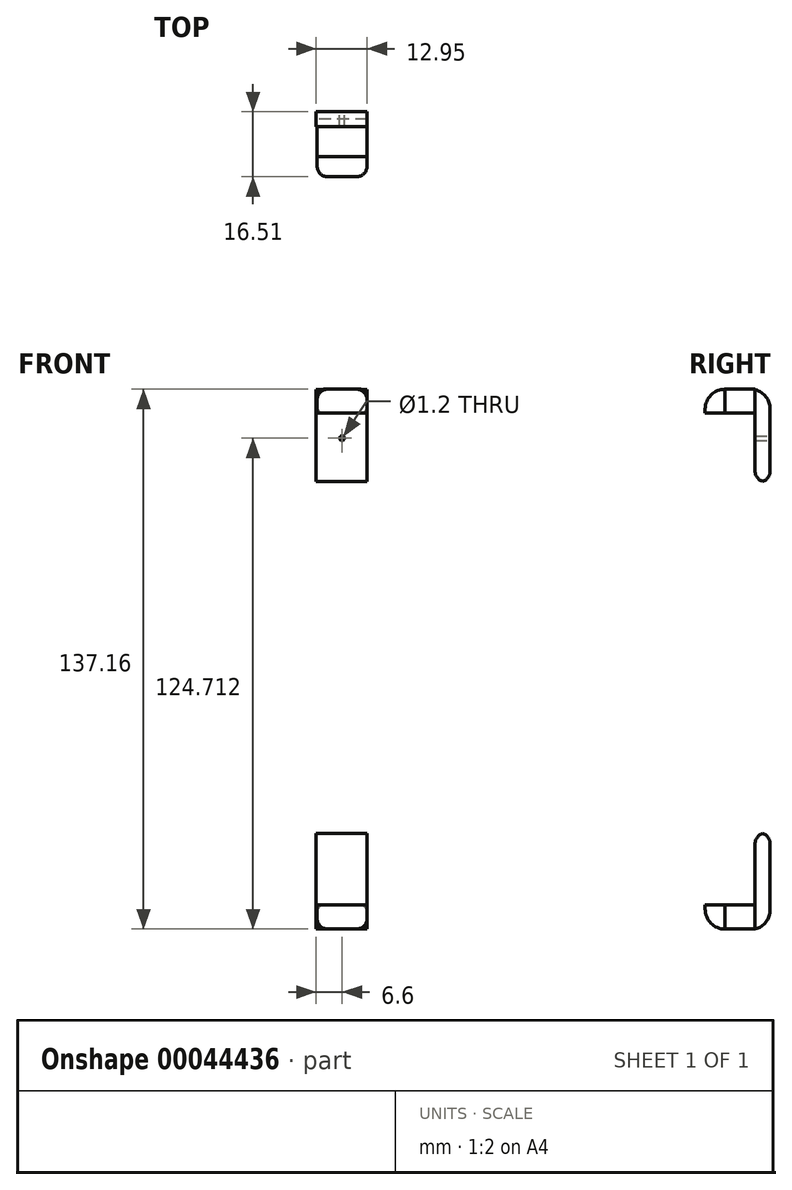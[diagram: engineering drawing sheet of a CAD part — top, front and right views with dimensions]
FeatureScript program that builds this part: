
annotation { "Feature Type Name" : "Feature", "Feature Type Description" : "" }
export const myFeature = defineFeature(function(context is Context, id is Id, definition is map)
    precondition{}
    {
        {
            var Q0;
            Q0=qCreatedBy(makeId("Front.planeOp"),FACE);
            var sketch = newSketch(context, id + "F0", { "sketchPlane" : qUnion([Q0])});
            skLineSegment(sketch, "E0.rect.bottom", {"start": v(-6.35, 68.58) * mm, "end": v(6.35, 68.58) * mm});
            skLineSegment(sketch, "E0.rect.top", {"start": v(-6.35, -68.58) * mm, "end": v(6.35, -68.58) * mm});
            skLineSegment(sketch, "E0.rect.left", {"start": v(-6.35, 68.58) * mm, "end": v(-6.35, -68.58) * mm});
            skLineSegment(sketch, "E0.rect.right", {"start": v(6.35, 68.58) * mm, "end": v(6.35, -68.58) * mm});
            skPoint(sketch, "E0.rect.middle", {"position": v(0, 0) * mm});
            skLineSegment(sketch, "E1.rect.bottom", {"start": v(0, 62.48) * mm, "end": v(0, 62.48) * mm});
            skLineSegment(sketch, "E1.rect.top", {"start": v(0, -62.48) * mm, "end": v(0, -62.48) * mm});
            skLineSegment(sketch, "E1.rect.left", {"start": v(0, 62.48) * mm, "end": v(0, -62.48) * mm});
            skLineSegment(sketch, "E1.rect.right", {"start": v(0, 62.48) * mm, "end": v(0, -62.48) * mm});
            skLineSegment(sketch, "E2", {"start": v(0, 62.48) * mm, "end": v(-6.35, 62.48) * mm});
            skLineSegment(sketch, "E3", {"start": v(-6.35, 62.48) * mm, "end": v(6.35, 62.48) * mm});
            skLineSegment(sketch, "E4", {"start": v(-6.35, -62.48) * mm, "end": v(6.35, -62.48) * mm});
            skSolve(sketch);
        }
        {
            var Q0;
            {var subQ4=sQuery(id+"F0.wireOp",EDGE,"E0.rect.top");Q0=makeQuery(id+"F0.imprint","IMPRINT",FACE,{"disambiguationData":[TD([[makeQuery(id+"F0.imprint","IMPRINT",EDGE,{"derivedFrom":subQ4}),1.0]])]});}
            var Q1;
            {var subQ4=sQuery(id+"F0.wireOp",EDGE,"E0.rect.bottom");Q1=makeQuery(id+"F0.imprint","IMPRINT",FACE,{"disambiguationData":[TD([[makeQuery(id+"F0.imprint","IMPRINT",EDGE,{"derivedFrom":subQ4}),-1.0]])]});}
            extrude(context, id + "F1", {"entities" : qUnion([Q0, Q1]), "oppositeDirection" : true, "depth" : 7.62 * mm});
        }
        {
            var Q0;
            {var subQ3=sQuery(id+"F0.wireOp",EDGE,"E1.rect.right");Q0=makeQuery(id+"F0.imprint","IMPRINT",FACE,{"disambiguationData":[TD([[makeQuery(id+"F0.imprint","IMPRINT",EDGE,{"derivedFrom":subQ3}),1.0]])]});}
            var Q1;
            {var subQ3=sQuery(id+"F0.wireOp",EDGE,"E1.rect.right");Q1=makeQuery(id+"F0.imprint","IMPRINT",FACE,{"disambiguationData":[TD([[makeQuery(id+"F0.imprint","IMPRINT",EDGE,{"derivedFrom":subQ3}),-1.0]])]});}
            var Q2;
            {var subQ4=sQuery(id+"F0.wireOp",EDGE,"E0.rect.top");Q2=makeQuery(id+"F0.imprint","IMPRINT",FACE,{"disambiguationData":[TD([[makeQuery(id+"F0.imprint","IMPRINT",EDGE,{"derivedFrom":subQ4}),1.0]])]});}
            var Q3;
            {var subQ4=sQuery(id+"F0.wireOp",EDGE,"E0.rect.bottom");Q3=makeQuery(id+"F0.imprint","IMPRINT",FACE,{"disambiguationData":[TD([[makeQuery(id+"F0.imprint","IMPRINT",EDGE,{"derivedFrom":subQ4}),-1.0]])]});}
            extrude(context, id + "F2", {"entities" : qUnion([Q0, Q1, Q2, Q3]), "depth" : 5.08 * mm});
        }
        {
            var Q0;
            Q0=makeQuery(id+"F1.opExtrude","CAP_FACE",FACE,{"disambiguationData":[OSD([sQuery(id+"F0.wireOp",EDGE,"E0.rect.top"),sQuery(id+"F0.wireOp",EDGE,"E0.rect.left"),sQuery(id+"F0.wireOp",EDGE,"E0.rect.right"),sQuery(id+"F0.wireOp",EDGE,"E4")])],"isStart":false});
            var sketch = newSketch(context, id + "F3", { "sketchPlane" : qUnion([Q0])});
            skLineSegment(sketch, "E5.bottom", {"start": v(-6.35, -68.58) * mm, "end": v(6.6, -68.58) * mm});
            skLineSegment(sketch, "E5.top", {"start": v(-6.35, 68.46) * mm, "end": v(6.6, 68.46) * mm});
            skLineSegment(sketch, "E5.left", {"start": v(-6.35, -68.58) * mm, "end": v(-6.35, 68.46) * mm});
            skLineSegment(sketch, "E5.right", {"start": v(6.6, -68.58) * mm, "end": v(6.6, 68.46) * mm});
            skLineSegment(sketch, "E6.bottom", {"start": v(-6.35, 45.07) * mm, "end": v(6.6, 45.07) * mm});
            skLineSegment(sketch, "E6.top", {"start": v(-6.35, -44.2) * mm, "end": v(6.6, -44.2) * mm});
            skLineSegment(sketch, "E6.left", {"start": v(-6.35, 45.07) * mm, "end": v(-6.35, -44.2) * mm});
            skLineSegment(sketch, "E6.right", {"start": v(6.6, 45.07) * mm, "end": v(6.6, -44.2) * mm});
            skSolve(sketch);
        }
        {
            var Q0;
            {var subQ7=sQuery(id+"F3.wireOp",EDGE,"E6.top");Q0=makeQuery(id+"F3.imprint","IMPRINT",FACE,{"disambiguationData":[TD([[makeQuery(id+"F3.imprint","IMPRINT",EDGE,{"derivedFrom":subQ7}),-1.0]])]});}
            var Q1;
            {var subQ0=sQuery(id+"F0.wireOp",EDGE,"E4");var subQ1=makeQuery(id+"F1.opExtrude","CAP_EDGE",EDGE,{"disambiguationData":[OSD([subQ0])],"isStart":false});Q1=makeQuery(id+"F3.imprint","IMPRINT",FACE,{"disambiguationData":[TD([[makeQuery(id+"F3.imprint","IMPRINT",EDGE,{"derivedFrom":subQ1}),1.0]])]});}
            var Q2;
            {var subQ2=sQuery(id+"F3.wireOp",EDGE,"E5.top");Q2=makeQuery(id+"F3.imprint","IMPRINT",FACE,{"disambiguationData":[TD([[makeQuery(id+"F3.imprint","IMPRINT",EDGE,{"derivedFrom":subQ2}),-1.0]])]});}
            extrude(context, id + "F4", {"entities" : qUnion([Q0, Q1, Q2]), "depth" : 3.8 * mm});
        }
        {
            var Q0;
            Q0=makeQuery(id+"F4.opExtrude","CAP_FACE",FACE,{"disambiguationData":[OSD([sQuery(id+"F3.wireOp",EDGE,"E5.top"),sQuery(id+"F3.wireOp",EDGE,"E5.left"),sQuery(id+"F3.wireOp",EDGE,"E5.right"),sQuery(id+"F3.wireOp",EDGE,"E6.bottom")])],"isStart":false});
            var sketch = newSketch(context, id + "F5", { "sketchPlane" : qUnion([Q0])});
            skLineSegment(sketch, "E7", {"start": v(0.1, 62.23) * mm, "end": v(0, 56.13) * mm});
            skCircle(sketch, "E8", {"center": v(0, 56.13) * mm, "radius": 0.6 * mm});
            skSolve(sketch);
        }
        {
            var Q0;
            Q0 = qSketchRegion(id + "F5", true);
            extrude(context, id + "F6", {"entities" : qUnion([Q0]), "operationType" : NewBodyOperationType.REMOVE, "oppositeDirection" : true, "depth" : 25.4 * mm});
        }
        {
            var Q0;
            Q0=makeQuery(id+"F4.opExtrude","CAP_EDGE",EDGE,{"disambiguationData":[OSD([sQuery(id+"F3.wireOp",EDGE,"E5.top")])],"isStart":false});
            var Q1;
            Q1=makeQuery(id+"F2.opExtrude","CAP_EDGE",EDGE,{"disambiguationData":[OSD([sQuery(id+"F0.wireOp",EDGE,"E0.rect.bottom")])],"isStart":false});
            var Q2;
            Q2=makeQuery(id+"F2.opExtrude","CAP_EDGE",EDGE,{"disambiguationData":[OSD([sQuery(id+"F0.wireOp",EDGE,"E0.rect.top")])],"isStart":false});
            var Q3;
            Q3=makeQuery(id+"F4.opExtrude","CAP_EDGE",EDGE,{"disambiguationData":[OSD([sQuery(id+"F3.wireOp",EDGE,"E5.bottom")])],"isStart":false});
            fillet(context, id + "F7", {"entities" : qUnion([Q0, Q1, Q2, Q3]), "radius" : 5.08 * mm, "tangentPropagation" : true, "allowEdgeOverflow" : false});
        }
        {
            var Q0;
            Q0=makeQuery(id+"F2.opExtrude","CAP_EDGE",EDGE,{"disambiguationData":[OSD([sQuery(id+"F0.wireOp",EDGE,"E0.rect.left")])],"isStart":false});
            var Q1;
            Q1=makeQuery(id+"F2.opExtrude","CAP_EDGE",EDGE,{"disambiguationData":[OSD([sQuery(id+"F0.wireOp",EDGE,"E0.rect.right")])],"isStart":false});
            var Q2;
            Q2=makeQuery(id+"F4.opExtrude","CAP_EDGE",EDGE,{"disambiguationData":[OSD([sQuery(id+"F3.wireOp",EDGE,"E6.bottom")])],"isStart":false});
            var Q3;
            Q3=makeQuery(id+"F4.opExtrude","CAP_EDGE",EDGE,{"disambiguationData":[OSD([sQuery(id+"F3.wireOp",EDGE,"E6.top")])],"isStart":false});
            var Q4;
            Q4=makeQuery(id+"F4.opExtrude","CAP_EDGE",EDGE,{"disambiguationData":[OSD([sQuery(id+"F3.wireOp",EDGE,"E6.top")])],"isStart":true});
            var Q5;
            Q5=makeQuery(id+"F4.opExtrude","CAP_EDGE",EDGE,{"disambiguationData":[OSD([sQuery(id+"F3.wireOp",EDGE,"E6.bottom")])],"isStart":true});
            fillet(context, id + "F8", {"entities" : qUnion([Q0, Q1, Q2, Q3, Q4, Q5]), "radius" : 2.67 * mm, "tangentPropagation" : true, "allowEdgeOverflow" : false});
        }
        {
            var Q0;
            Q0=makeQuery(id+"F1.opExtrude","SWEPT_EDGE",EDGE,{"disambiguationData":[OSD([sQuery(id+"F0.wireOp",EDGE,"E0.rect.bottom"),sQuery(id+"F0.wireOp",EDGE,"E0.rect.right")])]});
            var Q1;
            Q1=makeQuery(id+"F1.opExtrude","SWEPT_EDGE",EDGE,{"disambiguationData":[OSD([sQuery(id+"F0.wireOp",EDGE,"E0.rect.bottom"),sQuery(id+"F0.wireOp",EDGE,"E0.rect.left")])]});
            var Q2;
            Q2=makeQuery(id+"F1.opExtrude","SWEPT_EDGE",EDGE,{"disambiguationData":[OSD([sQuery(id+"F0.wireOp",EDGE,"E0.rect.right"),sQuery(id+"F0.wireOp",EDGE,"E3")])]});
            var Q3;
            Q3=makeQuery(id+"F1.opExtrude","SWEPT_EDGE",EDGE,{"disambiguationData":[OSD([sQuery(id+"F0.wireOp",EDGE,"E0.rect.top"),sQuery(id+"F0.wireOp",EDGE,"E0.rect.right")])]});
            var Q4;
            Q4=makeQuery(id+"F1.opExtrude","SWEPT_EDGE",EDGE,{"disambiguationData":[OSD([sQuery(id+"F0.wireOp",EDGE,"E0.rect.right"),sQuery(id+"F0.wireOp",EDGE,"E4")])]});
            var Q5;
            Q5=makeQuery(id+"F1.opExtrude","SWEPT_EDGE",EDGE,{"disambiguationData":[OSD([sQuery(id+"F0.wireOp",EDGE,"E0.rect.left"),sQuery(id+"F0.wireOp",EDGE,"E4")])]});
            var Q6;
            Q6=makeQuery(id+"F1.opExtrude","SWEPT_EDGE",EDGE,{"disambiguationData":[OSD([sQuery(id+"F0.wireOp",EDGE,"E0.rect.left"),sQuery(id+"F0.wireOp",EDGE,"E3")])]});
            var Q7;
            Q7=makeQuery(id+"F1.opExtrude","SWEPT_EDGE",EDGE,{"disambiguationData":[OSD([sQuery(id+"F0.wireOp",EDGE,"E0.rect.top"),sQuery(id+"F0.wireOp",EDGE,"E0.rect.left")])]});
            fillet(context, id + "F9", {"entities" : qUnion([Q0, Q1, Q2, Q3, Q4, Q5, Q6, Q7]), "radius" : 1.83 * mm, "tangentPropagation" : true, "allowEdgeOverflow" : false});
        }
    });
